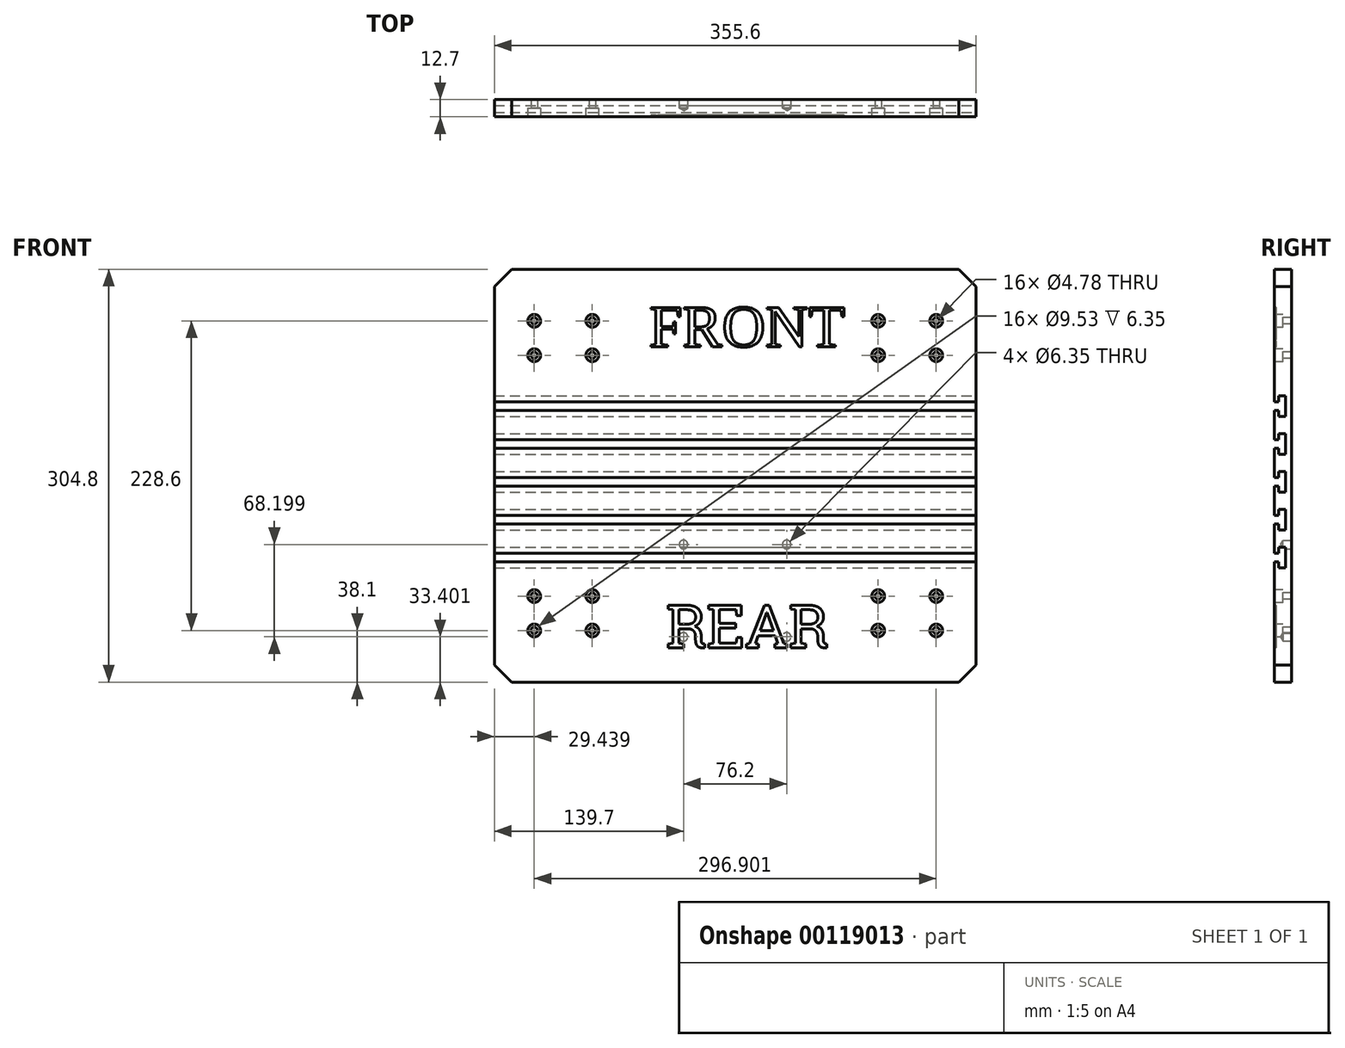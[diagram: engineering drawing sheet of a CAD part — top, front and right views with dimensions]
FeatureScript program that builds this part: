
annotation { "Feature Type Name" : "Feature", "Feature Type Description" : "" }
export const myFeature = defineFeature(function(context is Context, id is Id, definition is map)
    precondition{}
    {
        {
            var Q0;
            Q0=qCreatedBy(makeId("Front.planeOp"),FACE);
            var sketch = newSketch(context, id + "F0", { "sketchPlane" : qUnion([Q0])});
            skLineSegment(sketch, "E0.bottom", {"start": v(0, 0) * mm, "end": v(355.6, 0) * mm});
            skLineSegment(sketch, "E0.top", {"start": v(0, 304.8) * mm, "end": v(355.6, 304.8) * mm});
            skLineSegment(sketch, "E0.left", {"start": v(0, 0) * mm, "end": v(0, 304.8) * mm});
            skLineSegment(sketch, "E0.right", {"start": v(355.6, 0) * mm, "end": v(355.6, 304.8) * mm});
            skSolve(sketch);
        }
        {
            var Q0;
            Q0=makeQuery(id+"F0.imprint","IMPRINT",FACE,{"disambiguationData":[TD([[makeQuery(id+"F0.imprint","IMPRINT",EDGE,{"derivedFrom":sQuery(id+"F0.wireOp",EDGE,"E0.bottom")}),1.0]])]});
            extrude(context, id + "F1", {"entities" : qUnion([Q0]), "depth" : 12.7 * mm});
        }
        {
            var Q0;
            Q0=makeQuery(id+"F1.opExtrude","CAP_FACE",FACE,{"disambiguationData":[OSD([sQuery(id+"F0.wireOp",EDGE,"E0.bottom"),sQuery(id+"F0.wireOp",EDGE,"E0.top"),sQuery(id+"F0.wireOp",EDGE,"E0.left"),sQuery(id+"F0.wireOp",EDGE,"E0.right")])],"isStart":false});
            var sketch = newSketch(context, id + "F2", { "sketchPlane" : qUnion([Q0])});
            skLineSegment(sketch, "E1.bottom", {"start": v(72.31, 266.7) * mm, "end": v(283.46, 266.7) * mm, "construction": true});
            skLineSegment(sketch, "E1.top", {"start": v(72.31, 38.1) * mm, "end": v(283.46, 38.1) * mm, "construction": true});
            skLineSegment(sketch, "E1.left", {"start": v(72.31, 266.7) * mm, "end": v(72.31, 38.1) * mm, "construction": true});
            skLineSegment(sketch, "E1.right", {"start": v(283.46, 266.7) * mm, "end": v(283.46, 38.1) * mm, "construction": true});
            skPoint(sketch, "E2", {"position": v(72.31, 38.1) * mm});
            skPoint(sketch, "E3", {"position": v(72.31, 63.5) * mm});
            skPoint(sketch, "E4", {"position": v(72.31, 266.7) * mm});
            skPoint(sketch, "E5", {"position": v(72.31, 241.3) * mm});
            skPoint(sketch, "E6", {"position": v(283.46, 266.7) * mm});
            skPoint(sketch, "E7", {"position": v(283.46, 241.3) * mm});
            skPoint(sketch, "E8", {"position": v(283.46, 38.1) * mm});
            skPoint(sketch, "E9", {"position": v(283.46, 63.5) * mm});
            skPoint(sketch, "E10", {"position": v(29.44, 266.7) * mm});
            skPoint(sketch, "E11", {"position": v(29.44, 241.3) * mm});
            skPoint(sketch, "E12", {"position": v(29.44, 63.5) * mm});
            skPoint(sketch, "E13", {"position": v(29.44, 38.1) * mm});
            skPoint(sketch, "E14", {"position": v(326.34, 63.5) * mm});
            skPoint(sketch, "E15", {"position": v(326.34, 38.1) * mm});
            skPoint(sketch, "E16", {"position": v(326.34, 266.7) * mm});
            skPoint(sketch, "E17", {"position": v(326.34, 241.3) * mm});
            skSolve(sketch);
        }
        {
            var Q0;
            Q0=sQuery(id+"F2.wireOp",VERTEX,"E10");
            var Q1;
            Q1=sQuery(id+"F2.wireOp",VERTEX,"E4");
            var Q2;
            Q2=sQuery(id+"F2.wireOp",VERTEX,"E5");
            var Q3;
            Q3=sQuery(id+"F2.wireOp",VERTEX,"E11");
            var Q4;
            Q4=sQuery(id+"F2.wireOp",VERTEX,"E6");
            var Q5;
            Q5=sQuery(id+"F2.wireOp",VERTEX,"E16");
            var Q6;
            Q6=sQuery(id+"F2.wireOp",VERTEX,"E17");
            var Q7;
            Q7=sQuery(id+"F2.wireOp",VERTEX,"E7");
            var Q8;
            Q8=sQuery(id+"F2.wireOp",VERTEX,"E14");
            var Q9;
            Q9=sQuery(id+"F2.wireOp",VERTEX,"E9");
            var Q10;
            Q10=sQuery(id+"F2.wireOp",VERTEX,"E8");
            var Q11;
            Q11=sQuery(id+"F2.wireOp",VERTEX,"E15");
            var Q12;
            Q12=sQuery(id+"F2.wireOp",VERTEX,"E13");
            var Q13;
            Q13=sQuery(id+"F2.wireOp",VERTEX,"E2");
            var Q14;
            Q14=sQuery(id+"F2.wireOp",VERTEX,"E3");
            var Q15;
            Q15=sQuery(id+"F2.wireOp",VERTEX,"E12");
            var Q16;
            Q16=makeQuery(id+"F1.opExtrude","SWEPT_BODY",BODY,{"disambiguationData":[OSD([sQuery(id+"F0.wireOp",EDGE,"E0.bottom"),sQuery(id+"F0.wireOp",EDGE,"E0.top"),sQuery(id+"F0.wireOp",EDGE,"E0.left"),sQuery(id+"F0.wireOp",EDGE,"E0.right")])]});
            hole(context, id + "F3", {"style" : HoleStyle.C_BORE, "endStyle" : HoleEndStyle.THROUGH, "holeDiameter" : 4.78 * mm, "cBoreDiameter" : 9.52 * mm, "cBoreDepth" : 6.35 * mm, "locations" : qUnion([Q0, Q1, Q2, Q3, Q4, Q5, Q6, Q7, Q8, Q9, Q10, Q11, Q12, Q13, Q14, Q15]), "scope" : qUnion([Q16]), "isTappedThrough" : true});
        }
        {
            var Q0;
            Q0=makeQuery(id+"F1.opExtrude","SWEPT_FACE",FACE,{"disambiguationData":[OSD([sQuery(id+"F0.wireOp",EDGE,"E0.right")])]});
            var sketch = newSketch(context, id + "F4", { "sketchPlane" : qUnion([Q0])});
            skLineSegment(sketch, "E18", {"start": v(-12.7, 88.9) * mm, "end": v(-9.53, 88.9) * mm});
            skLineSegment(sketch, "E19", {"start": v(-9.53, 88.9) * mm, "end": v(-9.52, 84.45) * mm});
            skLineSegment(sketch, "E20", {"start": v(-9.52, 84.45) * mm, "end": v(-4.44, 84.45) * mm});
            skLineSegment(sketch, "E21", {"start": v(-4.44, 84.45) * mm, "end": v(-4.45, 99.7) * mm});
            skLineSegment(sketch, "E22", {"start": v(-4.45, 99.7) * mm, "end": v(-9.52, 99.7) * mm});
            skLineSegment(sketch, "E23", {"start": v(-9.52, 99.7) * mm, "end": v(-9.52, 95.25) * mm});
            skLineSegment(sketch, "E24", {"start": v(-9.52, 95.25) * mm, "end": v(-12.7, 95.25) * mm});
            skLineSegment(sketch, "E25", {"start": v(-12.7, 116.84) * mm, "end": v(-9.52, 116.84) * mm});
            skLineSegment(sketch, "E26", {"start": v(-9.52, 116.84) * mm, "end": v(-9.52, 112.4) * mm});
            skLineSegment(sketch, "E27", {"start": v(-9.52, 112.4) * mm, "end": v(-4.44, 112.4) * mm});
            skLineSegment(sketch, "E28", {"start": v(-4.44, 112.4) * mm, "end": v(-4.45, 127.64) * mm});
            skLineSegment(sketch, "E29", {"start": v(-4.45, 127.64) * mm, "end": v(-9.53, 127.64) * mm});
            skLineSegment(sketch, "E30", {"start": v(-9.53, 127.64) * mm, "end": v(-9.53, 123.2) * mm});
            skLineSegment(sketch, "E31", {"start": v(-9.53, 123.2) * mm, "end": v(-12.7, 123.2) * mm});
            skLineSegment(sketch, "E32", {"start": v(-12.7, 144.78) * mm, "end": v(-9.53, 144.78) * mm});
            skLineSegment(sketch, "E33", {"start": v(-9.53, 144.78) * mm, "end": v(-9.53, 140.33) * mm});
            skLineSegment(sketch, "E34", {"start": v(-9.52, 140.33) * mm, "end": v(-4.44, 140.33) * mm});
            skLineSegment(sketch, "E35", {"start": v(-4.44, 140.33) * mm, "end": v(-4.45, 155.57) * mm});
            skLineSegment(sketch, "E36", {"start": v(-4.45, 155.57) * mm, "end": v(-9.53, 155.57) * mm});
            skLineSegment(sketch, "E37", {"start": v(-9.53, 155.57) * mm, "end": v(-9.53, 151.13) * mm});
            skLineSegment(sketch, "E38", {"start": v(-9.53, 151.13) * mm, "end": v(-12.7, 151.13) * mm});
            skLineSegment(sketch, "E39", {"start": v(-12.7, 172.72) * mm, "end": v(-9.52, 172.72) * mm});
            skLineSegment(sketch, "E40", {"start": v(-9.52, 172.72) * mm, "end": v(-9.52, 168.27) * mm});
            skLineSegment(sketch, "E41", {"start": v(-9.52, 168.27) * mm, "end": v(-4.44, 168.27) * mm});
            skLineSegment(sketch, "E42", {"start": v(-4.44, 168.27) * mm, "end": v(-4.44, 183.51) * mm});
            skLineSegment(sketch, "E43", {"start": v(-4.44, 183.51) * mm, "end": v(-9.53, 183.51) * mm});
            skLineSegment(sketch, "E44", {"start": v(-9.53, 183.51) * mm, "end": v(-9.53, 179.07) * mm});
            skLineSegment(sketch, "E45", {"start": v(-9.53, 179.07) * mm, "end": v(-12.7, 179.07) * mm});
            skLineSegment(sketch, "E46", {"start": v(-12.7, 200.66) * mm, "end": v(-9.53, 200.66) * mm});
            skLineSegment(sketch, "E47", {"start": v(-9.53, 200.66) * mm, "end": v(-9.53, 196.21) * mm});
            skLineSegment(sketch, "E48", {"start": v(-9.53, 196.21) * mm, "end": v(-4.44, 196.21) * mm});
            skLineSegment(sketch, "E49", {"start": v(-4.44, 196.21) * mm, "end": v(-4.44, 211.45) * mm});
            skLineSegment(sketch, "E50", {"start": v(-4.45, 211.45) * mm, "end": v(-9.53, 211.45) * mm});
            skLineSegment(sketch, "E51", {"start": v(-9.53, 211.45) * mm, "end": v(-9.53, 207) * mm});
            skLineSegment(sketch, "E52", {"start": v(-9.53, 207) * mm, "end": v(-12.7, 207) * mm});
            skSolve(sketch);
        }
        {
            var Q0;
            {var subQ0=sQuery(id+"F4.wireOp",EDGE,"E46");Q0=makeQuery(id+"F4.imprint","IMPRINT",FACE,{"disambiguationData":[TD([[makeQuery(id+"F4.imprint","IMPRINT",EDGE,{"derivedFrom":subQ0}),1.0]])]});}
            var Q1;
            {var subQ0=sQuery(id+"F4.wireOp",EDGE,"E39");Q1=makeQuery(id+"F4.imprint","IMPRINT",FACE,{"disambiguationData":[TD([[makeQuery(id+"F4.imprint","IMPRINT",EDGE,{"derivedFrom":subQ0}),1.0]])]});}
            var Q2;
            {var subQ0=sQuery(id+"F4.wireOp",EDGE,"E32");Q2=makeQuery(id+"F4.imprint","IMPRINT",FACE,{"disambiguationData":[TD([[makeQuery(id+"F4.imprint","IMPRINT",EDGE,{"derivedFrom":subQ0}),1.0]])]});}
            var Q3;
            {var subQ0=sQuery(id+"F4.wireOp",EDGE,"E25");Q3=makeQuery(id+"F4.imprint","IMPRINT",FACE,{"disambiguationData":[TD([[makeQuery(id+"F4.imprint","IMPRINT",EDGE,{"derivedFrom":subQ0}),1.0]])]});}
            var Q4;
            {var subQ0=sQuery(id+"F4.wireOp",EDGE,"E18");Q4=makeQuery(id+"F4.imprint","IMPRINT",FACE,{"disambiguationData":[TD([[makeQuery(id+"F4.imprint","IMPRINT",EDGE,{"derivedFrom":subQ0}),1.0]])]});}
            extrude(context, id + "F5", {"entities" : qUnion([Q0, Q1, Q2, Q3, Q4]), "operationType" : NewBodyOperationType.REMOVE, "endBound" : BoundingType.THROUGH_ALL, "oppositeDirection" : true, "depth" : 25.4 * mm});
        }
        {
            var Q0;
            {var subQ0=sQuery(id+"F0.wireOp",EDGE,"E0.top");var subQ1=sQuery(id+"F0.wireOp",EDGE,"E0.left");var subQ2=sQuery(id+"F0.wireOp",EDGE,"E0.right");Q0=makeQuery(id+"F5.boolean.opBoolean","SPLIT",FACE,{"disambiguationData":[TD([makeQuery(id+"F1.opExtrude","SWEPT_FACE",FACE,{"disambiguationData":[OSD([subQ0])]})])],"derivedFrom":makeQuery(id+"F1.opExtrude","CAP_FACE",FACE,{"disambiguationData":[OSD([sQuery(id+"F0.wireOp",EDGE,"E0.bottom"),subQ0,subQ1,subQ2])],"isStart":false})});}
            var sketch = newSketch(context, id + "F6", { "sketchPlane" : qUnion([Q0])});
            skText(sketch, "E53", { "text": "FRONT", "fontName": "Tinos-Regular.ttf"});
            const initialGuessF6  = {"E53": [0.1143, 0.24765, 1, 0, 0.03175]};
            skSetInitialGuess(sketch, initialGuessF6);
            skSolve(sketch);
        }
        {
            var Q0;
            Q0 = qSketchRegion(id + "F6", true);
            extrude(context, id + "F7", {"entities" : qUnion([Q0]), "operationType" : NewBodyOperationType.REMOVE, "oppositeDirection" : true, "depth" : 1.27 * mm});
        }
        {
            var Q0;
            {var subQ0=sQuery(id+"F0.wireOp",EDGE,"E0.left");var subQ1=sQuery(id+"F0.wireOp",EDGE,"E0.bottom");var subQ2=sQuery(id+"F0.wireOp",EDGE,"E0.right");Q0=makeQuery(id+"F5.boolean.opBoolean","SPLIT",FACE,{"disambiguationData":[TD([makeQuery(id+"F1.opExtrude","SWEPT_FACE",FACE,{"disambiguationData":[OSD([subQ1])]})])],"derivedFrom":makeQuery(id+"F1.opExtrude","CAP_FACE",FACE,{"disambiguationData":[OSD([subQ1,sQuery(id+"F0.wireOp",EDGE,"E0.top"),subQ0,subQ2])],"isStart":false})});}
            var sketch = newSketch(context, id + "F8", { "sketchPlane" : qUnion([Q0])});
            skText(sketch, "E54", { "text": "REAR", "fontName": "RobotoSlab-Regular.ttf"});
            const initialGuessF8  = {"E54": [0.127, 0.0254, 1, 0, 0.03175]};
            skSetInitialGuess(sketch, initialGuessF8);
            skSolve(sketch);
        }
        {
            var Q0;
            Q0 = qSketchRegion(id + "F8", true);
            extrude(context, id + "F9", {"entities" : qUnion([Q0]), "operationType" : NewBodyOperationType.REMOVE, "oppositeDirection" : true, "depth" : 1.27 * mm});
        }
        {
            var Q0;
            Q0=makeQuery(id+"F1.opExtrude","CAP_FACE",FACE,{"disambiguationData":[OSD([sQuery(id+"F0.wireOp",EDGE,"E0.bottom"),sQuery(id+"F0.wireOp",EDGE,"E0.top"),sQuery(id+"F0.wireOp",EDGE,"E0.left"),sQuery(id+"F0.wireOp",EDGE,"E0.right")])],"isStart":true});
            var sketch = newSketch(context, id + "F10", { "sketchPlane" : qUnion([Q0])});
            skPoint(sketch, "E55", {"position": v(-215.9, 101.6) * mm});
            skPoint(sketch, "E56", {"position": v(-139.7, 101.6) * mm});
            skPoint(sketch, "E57", {"position": v(-215.9, 33.4) * mm});
            skPoint(sketch, "E58", {"position": v(-139.7, 33.4) * mm});
            skSolve(sketch);
        }
        {
            var Q0;
            Q0=sQuery(id+"F10.wireOp",VERTEX,"E55");
            var Q1;
            Q1=sQuery(id+"F10.wireOp",VERTEX,"E56");
            var Q2;
            Q2=sQuery(id+"F10.wireOp",VERTEX,"E58");
            var Q3;
            Q3=sQuery(id+"F10.wireOp",VERTEX,"E57");
            var Q4;
            Q4=makeQuery(id+"F1.opExtrude","SWEPT_BODY",BODY,{"disambiguationData":[OSD([sQuery(id+"F0.wireOp",EDGE,"E0.bottom"),sQuery(id+"F0.wireOp",EDGE,"E0.top"),sQuery(id+"F0.wireOp",EDGE,"E0.left"),sQuery(id+"F0.wireOp",EDGE,"E0.right")])]});
            hole(context, id + "F11", {"style" : HoleStyle.SIMPLE, "endStyle" : HoleEndStyle.BLIND, "holeDiameter" : 6.35 * mm, "holeDepth" : 6.35 * mm, "locations" : qUnion([Q0, Q1, Q2, Q3]), "scope" : qUnion([Q4])});
        }
        {
            var Q0;
            Q0=makeQuery(id+"F1.opExtrude","SWEPT_EDGE",EDGE,{"disambiguationData":[OSD([sQuery(id+"F0.wireOp",EDGE,"E0.top"),sQuery(id+"F0.wireOp",EDGE,"E0.left")])]});
            var Q1;
            Q1=makeQuery(id+"F1.opExtrude","SWEPT_EDGE",EDGE,{"disambiguationData":[OSD([sQuery(id+"F0.wireOp",EDGE,"E0.top"),sQuery(id+"F0.wireOp",EDGE,"E0.right")])]});
            var Q2;
            Q2=makeQuery(id+"F1.opExtrude","SWEPT_EDGE",EDGE,{"disambiguationData":[OSD([sQuery(id+"F0.wireOp",EDGE,"E0.bottom"),sQuery(id+"F0.wireOp",EDGE,"E0.right")])]});
            var Q3;
            Q3=makeQuery(id+"F1.opExtrude","SWEPT_EDGE",EDGE,{"disambiguationData":[OSD([sQuery(id+"F0.wireOp",EDGE,"E0.bottom"),sQuery(id+"F0.wireOp",EDGE,"E0.left")])]});
            chamfer(context, id + "F12", {"entities" : qUnion([Q0, Q1, Q2, Q3]), "width" : 12.7 * mm, "tangentPropagation" : true});
        }
    });
